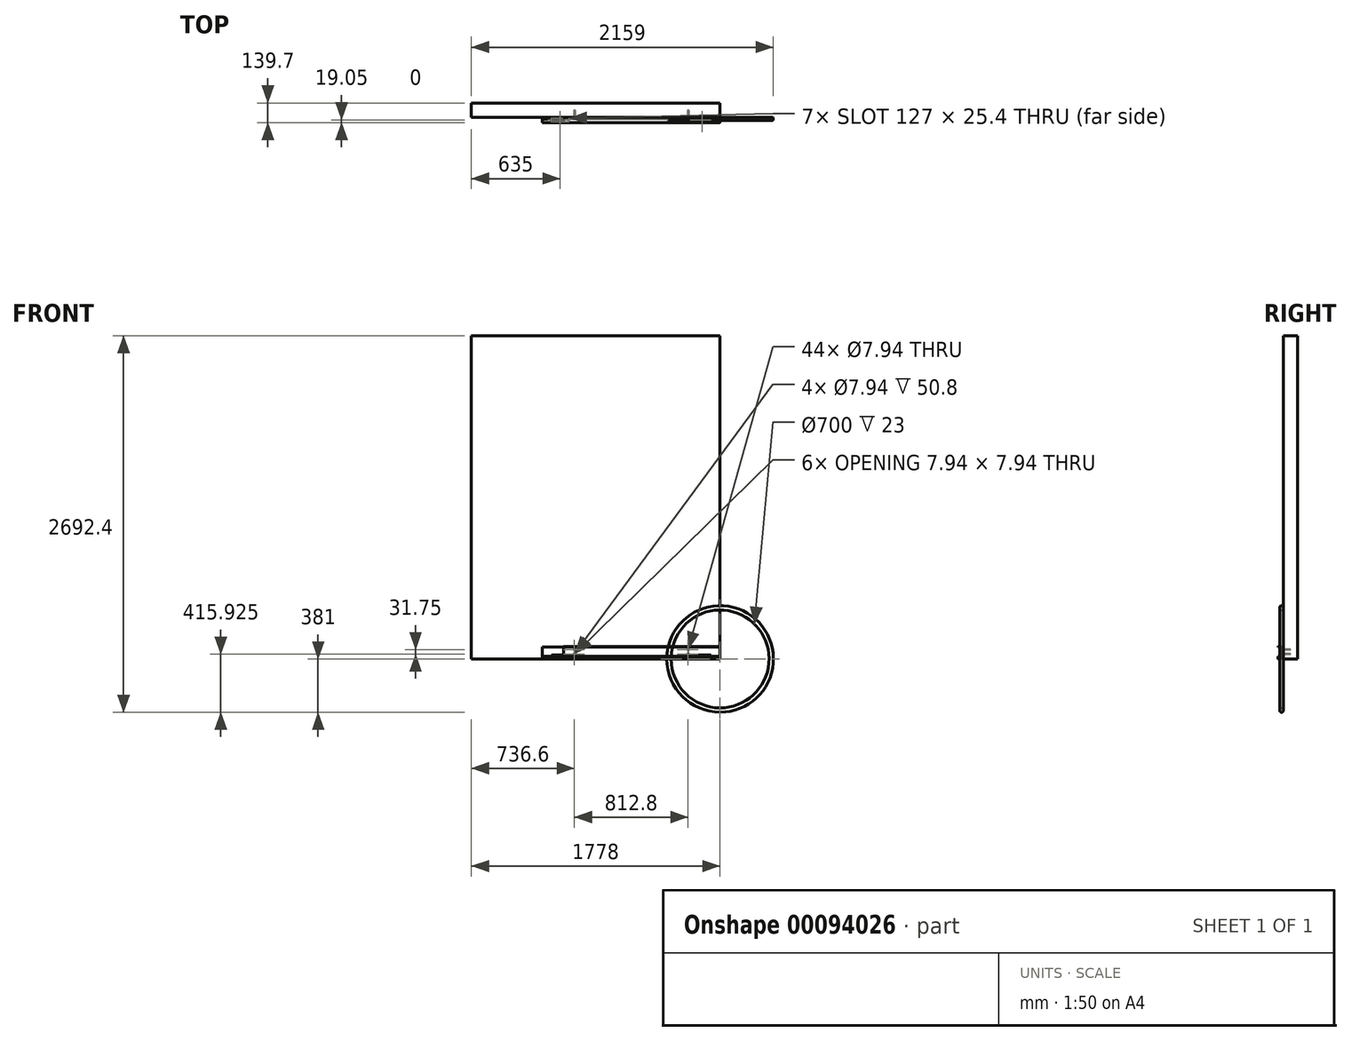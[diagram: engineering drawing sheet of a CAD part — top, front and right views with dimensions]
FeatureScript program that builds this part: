
annotation { "Feature Type Name" : "Feature", "Feature Type Description" : "" }
export const myFeature = defineFeature(function(context is Context, id is Id, definition is map)
    precondition{}
    {
        {
            var Q0;
            Q0=qCreatedBy(makeId("Right.planeOp"),FACE);
            var sketch = newSketch(context, id + "F0", { "sketchPlane" : qUnion([Q0])});
            skLineSegment(sketch, "E0", {"start": v(0, 3.17) * mm, "end": v(0, 85.73) * mm});
            skLineSegment(sketch, "E1", {"start": v(-3.18, 88.9) * mm, "end": v(-12.7, 88.9) * mm, "construction": true});
            skLineSegment(sketch, "E2", {"start": v(-12.7, 88.9) * mm, "end": v(-12.7, 85.73) * mm, "construction": true});
            skLineSegment(sketch, "E3", {"start": v(-25.4, 19.05) * mm, "end": v(-38.1, 19.05) * mm});
            skLineSegment(sketch, "E4", {"start": v(-38.1, 19.05) * mm, "end": v(-38.1, 3.18) * mm});
            skLineSegment(sketch, "E5", {"start": v(-34.92, 0) * mm, "end": v(-3.17, 0) * mm, "construction": true});
            skPoint(sketch, "E6.visualSharp", {"position": v(-12.7, 19.05) * mm});
            skArc(sketch, "E6.filletArc", {"start": v(-25.4, 19.05) * mm, "mid": v(-16.42, 22.77) * mm, "end": v(-12.7, 31.75) * mm});
            skPoint(sketch, "E7.visualSharp", {"position": v(-38.1, 0) * mm});
            skArc(sketch, "E7.filletArc", {"start": v(-38.1, 3.18) * mm, "mid": v(-37.17, 0.93) * mm, "end": v(-34.92, 0) * mm, "construction": true});
            skPoint(sketch, "E8.visualSharp", {"position": v(0, 0) * mm});
            skArc(sketch, "E8.filletArc", {"start": v(-3.18, 0) * mm, "mid": v(-0.93, 0.93) * mm, "end": v(0, 3.17) * mm, "construction": true});
            skPoint(sketch, "E9.visualSharp", {"position": v(0, 88.9) * mm});
            skArc(sketch, "E9.filletArc", {"start": v(0, 85.73) * mm, "mid": v(-0.93, 87.97) * mm, "end": v(-3.18, 88.9) * mm, "construction": true});
            skLineSegment(sketch, "E10", {"start": v(0, 85.73) * mm, "end": v(-12.7, 85.73) * mm});
            skLineSegment(sketch, "E11", {"start": v(-12.7, 85.73) * mm, "end": v(-12.7, 31.75) * mm});
            skLineSegment(sketch, "E12", {"start": v(-38.1, 3.18) * mm, "end": v(0, 3.17) * mm});
            skSolve(sketch);
        }
        {
            var Q0;
            Q0=makeQuery(id+"F0.imprint","IMPRINT",FACE,{"disambiguationData":[TD([[makeQuery(id+"F0.imprint","IMPRINT",EDGE,{"derivedFrom":sQuery(id+"F0.wireOp",EDGE,"E0")}),1.0]])]});
            extrude(context, id + "F1", {"entities" : qUnion([Q0]), "oppositeDirection" : true, "depth" : 1270 * mm});
        }
        {
            var Q0;
            Q0=qCreatedBy(makeId("Right.planeOp"),FACE);
            var sketch = newSketch(context, id + "F2", { "sketchPlane" : qUnion([Q0])});
            skLineSegment(sketch, "E13.bottom", {"start": v(-3.18, 0) * mm, "end": v(-34.93, 0) * mm});
            skLineSegment(sketch, "E13.top", {"start": v(-3.18, 88.9) * mm, "end": v(-34.93, 88.9) * mm});
            skLineSegment(sketch, "E13.left", {"start": v(0, 3.18) * mm, "end": v(0, 85.73) * mm});
            skLineSegment(sketch, "E13.right", {"start": v(-38.1, 3.18) * mm, "end": v(-38.1, 85.73) * mm});
            skPoint(sketch, "E14.visualSharp", {"position": v(-38.1, 88.9) * mm});
            skArc(sketch, "E14.filletArc", {"start": v(-34.93, 88.9) * mm, "mid": v(-37.17, 87.97) * mm, "end": v(-38.1, 85.73) * mm});
            skPoint(sketch, "E15.visualSharp", {"position": v(0, 88.9) * mm});
            skArc(sketch, "E15.filletArc", {"start": v(0, 85.73) * mm, "mid": v(-0.93, 87.97) * mm, "end": v(-3.18, 88.9) * mm});
            skPoint(sketch, "E16.visualSharp", {"position": v(0, 0) * mm});
            skArc(sketch, "E16.filletArc", {"start": v(-3.18, 0) * mm, "mid": v(-0.93, 0.93) * mm, "end": v(0, 3.18) * mm});
            skPoint(sketch, "E17.visualSharp", {"position": v(-38.1, 0) * mm});
            skArc(sketch, "E17.filletArc", {"start": v(-38.1, 3.17) * mm, "mid": v(-37.17, 0.93) * mm, "end": v(-34.93, 0) * mm});
            skSolve(sketch);
        }
        {
            var Q0;
            Q0 = qSketchRegion(id + "F2", true);
            extrude(context, id + "F3", {"entities" : qUnion([Q0]), "oppositeDirection" : true, "depth" : 1117.6 * mm});
        }
        {
            var Q0;
            Q0=qCreatedBy(makeId("Right.planeOp"),FACE);
            var sketch = newSketch(context, id + "F4", { "sketchPlane" : qUnion([Q0])});
            skLineSegment(sketch, "E18.bottom", {"start": v(-3.18, 0) * mm, "end": v(-34.93, 0) * mm, "construction": true});
            skLineSegment(sketch, "E18.top", {"start": v(-3.18, 88.9) * mm, "end": v(-34.93, 88.9) * mm, "construction": true});
            skLineSegment(sketch, "E18.left", {"start": v(0, 3.17) * mm, "end": v(0, 85.73) * mm});
            skLineSegment(sketch, "E18.right", {"start": v(-38.1, 3.17) * mm, "end": v(-38.1, 85.73) * mm});
            skPoint(sketch, "E19.visualSharp", {"position": v(-38.1, 88.9) * mm});
            skArc(sketch, "E19.filletArc", {"start": v(-34.93, 88.9) * mm, "mid": v(-37.17, 87.97) * mm, "end": v(-38.1, 85.73) * mm, "construction": true});
            skPoint(sketch, "E20.visualSharp", {"position": v(0, 88.9) * mm});
            skArc(sketch, "E20.filletArc", {"start": v(0, 85.73) * mm, "mid": v(-0.93, 87.97) * mm, "end": v(-3.18, 88.9) * mm, "construction": true});
            skPoint(sketch, "E21.visualSharp", {"position": v(0, 0) * mm});
            skArc(sketch, "E21.filletArc", {"start": v(-3.18, 0) * mm, "mid": v(-0.93, 0.93) * mm, "end": v(0, 3.17) * mm, "construction": true});
            skPoint(sketch, "E22.visualSharp", {"position": v(-38.1, 0) * mm});
            skArc(sketch, "E22.filletArc", {"start": v(-38.1, 3.17) * mm, "mid": v(-37.17, 0.93) * mm, "end": v(-34.93, 0) * mm, "construction": true});
            skLineSegment(sketch, "E23", {"start": v(-38.1, 85.73) * mm, "end": v(0, 85.73) * mm});
            skLineSegment(sketch, "E24", {"start": v(-38.1, 3.17) * mm, "end": v(0, 3.17) * mm});
            skSolve(sketch);
        }
        {
            var Q0;
            Q0 = qSketchRegion(id + "F4", true);
            extrude(context, id + "F5", {"entities" : qUnion([Q0]), "oppositeDirection" : true, "depth" : 1117.6 * mm});
        }
        {
            var Q0;
            Q0=makeQuery(id+"F5.opExtrude","SWEPT_BODY",BODY,{"disambiguationData":[OSD([sQuery(id+"F4.wireOp",EDGE,"E18.left"),sQuery(id+"F4.wireOp",EDGE,"E18.right"),sQuery(id+"F4.wireOp",EDGE,"E23"),sQuery(id+"F4.wireOp",EDGE,"E24")])]});
            transform(context, id + "F6", {"entities" : qUnion([Q0]), "transformType" : TransformType.TRANSLATION_3D, "dx" : 0 * mm, "dy" : 0 * mm, "dz" : 0 * mm, "makeCopy" : true});
        }
        {
            var Q0;
            Q0=makeQuery(id+"F6.opPattern","COPY",FACE,{"derivedFrom":makeQuery(id+"F5.opExtrude","CAP_FACE",FACE,{"disambiguationData":[OSD([sQuery(id+"F4.wireOp",EDGE,"E18.left"),sQuery(id+"F4.wireOp",EDGE,"E18.right"),sQuery(id+"F4.wireOp",EDGE,"E23"),sQuery(id+"F4.wireOp",EDGE,"E24")])],"isStart":true}),"instanceName":"1"});
            var sketch = newSketch(context, id + "F7", { "sketchPlane" : qUnion([Q0])});
            skLineSegment(sketch, "E25", {"start": v(-38.1, 3.17) * mm, "end": v(-38.1, 31.75) * mm, "construction": true});
            skLineSegment(sketch, "E26", {"start": v(-38.1, 31.75) * mm, "end": v(-14.29, 31.75) * mm});
            skLineSegment(sketch, "E27", {"start": v(-14.29, 31.75) * mm, "end": v(-14.29, 85.73) * mm});
            skLineSegment(sketch, "E28", {"start": v(-14.29, 85.73) * mm, "end": v(-38.1, 85.73) * mm});
            skLineSegment(sketch, "E29", {"start": v(-38.1, 85.73) * mm, "end": v(-38.1, 31.75) * mm});
            skSolve(sketch);
        }
        {
            var Q0;
            Q0 = qSketchRegion(id + "F7", true);
            extrude(context, id + "F8", {"entities" : qUnion([Q0]), "operationType" : NewBodyOperationType.REMOVE, "endBound" : BoundingType.THROUGH_ALL, "oppositeDirection" : true, "depth" : 25.4 * mm});
        }
        {
            var Q0;
            Q0=makeQuery(id+"F1.opExtrude","SWEPT_BODY",BODY,{"disambiguationData":[OSD([sQuery(id+"F0.wireOp",EDGE,"E0"),sQuery(id+"F0.wireOp",EDGE,"E3"),sQuery(id+"F0.wireOp",EDGE,"E4"),sQuery(id+"F0.wireOp",EDGE,"E6.filletArc"),sQuery(id+"F0.wireOp",EDGE,"E10"),sQuery(id+"F0.wireOp",EDGE,"E11"),sQuery(id+"F0.wireOp",EDGE,"E12")])]});
            transform(context, id + "F9", {"entities" : qUnion([Q0]), "transformType" : TransformType.TRANSLATION_3D, "dx" : 0 * mm, "dy" : 0 * mm, "dz" : 0 * mm, "makeCopy" : true});
        }
        {
            var Q0;
            Q0=makeQuery(id+"F9.opPattern","COPY",FACE,{"derivedFrom":makeQuery(id+"F1.opExtrude","CAP_FACE",FACE,{"disambiguationData":[OSD([sQuery(id+"F0.wireOp",EDGE,"E0"),sQuery(id+"F0.wireOp",EDGE,"E3"),sQuery(id+"F0.wireOp",EDGE,"E4"),sQuery(id+"F0.wireOp",EDGE,"E6.filletArc"),sQuery(id+"F0.wireOp",EDGE,"E10"),sQuery(id+"F0.wireOp",EDGE,"E11"),sQuery(id+"F0.wireOp",EDGE,"E12")])],"isStart":true}),"instanceName":"1"});
            var sketch = newSketch(context, id + "F10", { "sketchPlane" : qUnion([Q0])});
            skLineSegment(sketch, "E30", {"start": v(-25.4, 19.05) * mm, "end": v(-12.7, 19.05) * mm});
            skLineSegment(sketch, "E31", {"start": v(-12.7, 19.05) * mm, "end": v(-12.7, 31.75) * mm});
            skLineSegment(sketch, "E32", {"start": v(-12.7, 31.75) * mm, "end": v(-25.4, 31.75) * mm});
            skLineSegment(sketch, "E33", {"start": v(-25.4, 31.75) * mm, "end": v(-25.4, 19.05) * mm});
            skSolve(sketch);
        }
        {
            var Q0;
            Q0 = qSketchRegion(id + "F10", true);
            extrude(context, id + "F11", {"entities" : qUnion([Q0]), "operationType" : NewBodyOperationType.REMOVE, "endBound" : BoundingType.THROUGH_ALL, "oppositeDirection" : true, "depth" : 25.4 * mm});
        }
        {
            var Q0;
            Q0=makeQuery(id+"F1.opExtrude","SWEPT_BODY",BODY,{"disambiguationData":[OSD([sQuery(id+"F0.wireOp",EDGE,"E0"),sQuery(id+"F0.wireOp",EDGE,"E3"),sQuery(id+"F0.wireOp",EDGE,"E4"),sQuery(id+"F0.wireOp",EDGE,"E6.filletArc"),sQuery(id+"F0.wireOp",EDGE,"E10"),sQuery(id+"F0.wireOp",EDGE,"E11"),sQuery(id+"F0.wireOp",EDGE,"E12")])]});
            transform(context, id + "F12", {"entities" : qUnion([Q0]), "transformType" : TransformType.TRANSLATION_3D, "dx" : 0 * mm, "dy" : 0 * mm, "dz" : 0 * mm, "makeCopy" : true});
        }
        {
            var Q0;
            Q0=makeQuery(id+"F12.opPattern","COPY",FACE,{"derivedFrom":makeQuery(id+"F1.opExtrude","CAP_FACE",FACE,{"disambiguationData":[OSD([sQuery(id+"F0.wireOp",EDGE,"E0"),sQuery(id+"F0.wireOp",EDGE,"E3"),sQuery(id+"F0.wireOp",EDGE,"E4"),sQuery(id+"F0.wireOp",EDGE,"E6.filletArc"),sQuery(id+"F0.wireOp",EDGE,"E10"),sQuery(id+"F0.wireOp",EDGE,"E11"),sQuery(id+"F0.wireOp",EDGE,"E12")])],"isStart":true}),"instanceName":"1"});
            var sketch = newSketch(context, id + "F13", { "sketchPlane" : qUnion([Q0])});
            skLineSegment(sketch, "E34", {"start": v(-25.4, 19.05) * mm, "end": v(-19.05, 19.05) * mm});
            skLineSegment(sketch, "E35", {"start": v(-12.7, 25.4) * mm, "end": v(-12.7, 31.75) * mm});
            skLineSegment(sketch, "E36", {"start": v(-12.7, 31.75) * mm, "end": v(-25.4, 31.75) * mm});
            skLineSegment(sketch, "E37", {"start": v(-25.4, 31.75) * mm, "end": v(-25.4, 19.05) * mm});
            skPoint(sketch, "E38.visualSharp", {"position": v(-12.7, 19.05) * mm});
            skArc(sketch, "E38.filletArc", {"start": v(-19.05, 19.05) * mm, "mid": v(-14.56, 20.9) * mm, "end": v(-12.7, 25.4) * mm});
            skSolve(sketch);
        }
        {
            var Q0;
            Q0 = qSketchRegion(id + "F13", true);
            extrude(context, id + "F14", {"entities" : qUnion([Q0]), "operationType" : NewBodyOperationType.REMOVE, "endBound" : BoundingType.THROUGH_ALL, "oppositeDirection" : true, "depth" : 25.4 * mm});
        }
        {
            var Q0;
            Q0=makeQuery(id+"F6.opPattern","COPY",BODY,{"derivedFrom":makeQuery(id+"F5.opExtrude","SWEPT_BODY",BODY,{"disambiguationData":[OSD([sQuery(id+"F4.wireOp",EDGE,"E18.left"),sQuery(id+"F4.wireOp",EDGE,"E18.right"),sQuery(id+"F4.wireOp",EDGE,"E23"),sQuery(id+"F4.wireOp",EDGE,"E24")])]}),"instanceName":"1"});
            transform(context, id + "F15", {"entities" : qUnion([Q0]), "transformType" : TransformType.TRANSLATION_3D, "dx" : 0 * mm, "dy" : 0 * mm, "dz" : 0 * mm, "makeCopy" : true});
        }
        {
            var Q0;
            Q0=makeQuery(id+"F15.opPattern","COPY",FACE,{"derivedFrom":makeQuery(id+"F6.opPattern","COPY",FACE,{"derivedFrom":makeQuery(id+"F5.opExtrude","CAP_FACE",FACE,{"disambiguationData":[OSD([sQuery(id+"F4.wireOp",EDGE,"E18.left"),sQuery(id+"F4.wireOp",EDGE,"E18.right"),sQuery(id+"F4.wireOp",EDGE,"E23"),sQuery(id+"F4.wireOp",EDGE,"E24")])],"isStart":true}),"instanceName":"1"}),"instanceName":"1"});
            var sketch = newSketch(context, id + "F16", { "sketchPlane" : qUnion([Q0])});
            skCircle(sketch, "E39", {"center": v(-38.1, 31.75) * mm, "radius": 12.7 * mm});
            skSolve(sketch);
        }
        {
            var Q0;
            Q0 = qSketchRegion(id + "F16", true);
            extrude(context, id + "F17", {"entities" : qUnion([Q0]), "operationType" : NewBodyOperationType.REMOVE, "endBound" : BoundingType.THROUGH_ALL, "oppositeDirection" : true, "depth" : 25.4 * mm});
        }
        {
            var Q0;
            Q0=makeQuery(id+"F15.opPattern","COPY",BODY,{"derivedFrom":makeQuery(id+"F6.opPattern","COPY",BODY,{"derivedFrom":makeQuery(id+"F5.opExtrude","SWEPT_BODY",BODY,{"disambiguationData":[OSD([sQuery(id+"F4.wireOp",EDGE,"E18.left"),sQuery(id+"F4.wireOp",EDGE,"E18.right"),sQuery(id+"F4.wireOp",EDGE,"E23"),sQuery(id+"F4.wireOp",EDGE,"E24")])]}),"instanceName":"1"}),"instanceName":"1"});
            transform(context, id + "F18", {"entities" : qUnion([Q0]), "transformType" : TransformType.TRANSLATION_3D, "dx" : 0 * mm, "dy" : 0 * mm, "dz" : 0 * mm, "makeCopy" : true});
        }
        {
            var Q0;
            Q0=makeQuery(id+"F18.opPattern","COPY",FACE,{"derivedFrom":makeQuery(id+"F15.opPattern","COPY",FACE,{"derivedFrom":makeQuery(id+"F6.opPattern","COPY",FACE,{"derivedFrom":makeQuery(id+"F5.opExtrude","CAP_FACE",FACE,{"disambiguationData":[OSD([sQuery(id+"F4.wireOp",EDGE,"E18.left"),sQuery(id+"F4.wireOp",EDGE,"E18.right"),sQuery(id+"F4.wireOp",EDGE,"E23"),sQuery(id+"F4.wireOp",EDGE,"E24")])],"isStart":true}),"instanceName":"1"}),"instanceName":"1"}),"instanceName":"1"});
            var sketch = newSketch(context, id + "F19", { "sketchPlane" : qUnion([Q0])});
            skCircle(sketch, "E40", {"center": v(-25.4, 31.75) * mm, "radius": 12.7 * mm});
            skSolve(sketch);
        }
        {
            var Q0;
            Q0 = qSketchRegion(id + "F19", true);
            extrude(context, id + "F20", {"entities" : qUnion([Q0]), "operationType" : NewBodyOperationType.REMOVE, "endBound" : BoundingType.THROUGH_ALL, "oppositeDirection" : true, "depth" : 25.4 * mm});
        }
        {
            var Q0;
            Q0=makeQuery(id+"F18.opPattern","COPY",BODY,{"derivedFrom":makeQuery(id+"F15.opPattern","COPY",BODY,{"derivedFrom":makeQuery(id+"F6.opPattern","COPY",BODY,{"derivedFrom":makeQuery(id+"F5.opExtrude","SWEPT_BODY",BODY,{"disambiguationData":[OSD([sQuery(id+"F4.wireOp",EDGE,"E18.left"),sQuery(id+"F4.wireOp",EDGE,"E18.right"),sQuery(id+"F4.wireOp",EDGE,"E23"),sQuery(id+"F4.wireOp",EDGE,"E24")])]}),"instanceName":"1"}),"instanceName":"1"}),"instanceName":"1"});
            transform(context, id + "F21", {"entities" : qUnion([Q0]), "transformType" : TransformType.TRANSLATION_3D, "dx" : 0 * mm, "dy" : 0 * mm, "dz" : 0 * mm, "makeCopy" : true});
        }
        {
            var Q0;
            Q0=makeQuery(id+"F21.opPattern","COPY",FACE,{"derivedFrom":makeQuery(id+"F18.opPattern","COPY",FACE,{"derivedFrom":makeQuery(id+"F15.opPattern","COPY",FACE,{"derivedFrom":makeQuery(id+"F6.opPattern","COPY",FACE,{"derivedFrom":makeQuery(id+"F5.opExtrude","CAP_FACE",FACE,{"disambiguationData":[OSD([sQuery(id+"F4.wireOp",EDGE,"E18.left"),sQuery(id+"F4.wireOp",EDGE,"E18.right"),sQuery(id+"F4.wireOp",EDGE,"E23"),sQuery(id+"F4.wireOp",EDGE,"E24")])],"isStart":true}),"instanceName":"1"}),"instanceName":"1"}),"instanceName":"1"}),"instanceName":"1"});
            var sketch = newSketch(context, id + "F22", { "sketchPlane" : qUnion([Q0])});
            skLineSegment(sketch, "E41", {"start": v(-38.1, 19.05) * mm, "end": v(-25.4, 19.05) * mm});
            skLineSegment(sketch, "E42", {"start": v(-25.4, 19.05) * mm, "end": v(-25.4, 31.75) * mm});
            skLineSegment(sketch, "E43", {"start": v(-38.1, 19.05) * mm, "end": v(-38.1, 31.75) * mm});
            skLineSegment(sketch, "E44", {"start": v(-38.1, 31.75) * mm, "end": v(-25.4, 31.75) * mm});
            skSolve(sketch);
        }
        {
            var Q0;
            Q0 = qSketchRegion(id + "F22", true);
            extrude(context, id + "F23", {"entities" : qUnion([Q0]), "operationType" : NewBodyOperationType.REMOVE, "endBound" : BoundingType.THROUGH_ALL, "oppositeDirection" : true, "depth" : 25.4 * mm});
        }
        {
            var Q0;
            Q0=makeQuery(id+"F21.opPattern","COPY",BODY,{"derivedFrom":makeQuery(id+"F18.opPattern","COPY",BODY,{"derivedFrom":makeQuery(id+"F15.opPattern","COPY",BODY,{"derivedFrom":makeQuery(id+"F6.opPattern","COPY",BODY,{"derivedFrom":makeQuery(id+"F5.opExtrude","SWEPT_BODY",BODY,{"disambiguationData":[OSD([sQuery(id+"F4.wireOp",EDGE,"E18.left"),sQuery(id+"F4.wireOp",EDGE,"E18.right"),sQuery(id+"F4.wireOp",EDGE,"E23"),sQuery(id+"F4.wireOp",EDGE,"E24")])]}),"instanceName":"1"}),"instanceName":"1"}),"instanceName":"1"}),"instanceName":"1"});
            transform(context, id + "F24", {"entities" : qUnion([Q0]), "transformType" : TransformType.TRANSLATION_3D, "dx" : 0 * mm, "dy" : 0 * mm, "dz" : 0 * mm, "makeCopy" : true});
        }
        {
            var Q0;
            Q0=makeQuery(id+"F24.opPattern","COPY",FACE,{"derivedFrom":makeQuery(id+"F21.opPattern","COPY",FACE,{"derivedFrom":makeQuery(id+"F18.opPattern","COPY",FACE,{"derivedFrom":makeQuery(id+"F15.opPattern","COPY",FACE,{"derivedFrom":makeQuery(id+"F6.opPattern","COPY",FACE,{"derivedFrom":makeQuery(id+"F5.opExtrude","CAP_FACE",FACE,{"disambiguationData":[OSD([sQuery(id+"F4.wireOp",EDGE,"E18.left"),sQuery(id+"F4.wireOp",EDGE,"E18.right"),sQuery(id+"F4.wireOp",EDGE,"E23"),sQuery(id+"F4.wireOp",EDGE,"E24")])],"isStart":true}),"instanceName":"1"}),"instanceName":"1"}),"instanceName":"1"}),"instanceName":"1"}),"instanceName":"1"});
            var sketch = newSketch(context, id + "F25", { "sketchPlane" : qUnion([Q0])});
            skLineSegment(sketch, "E45.bottom", {"start": v(-14.29, 85.73) * mm, "end": v(-12.7, 85.73) * mm});
            skLineSegment(sketch, "E45.top", {"start": v(-14.29, 31.75) * mm, "end": v(-12.7, 31.75) * mm});
            skLineSegment(sketch, "E45.left", {"start": v(-14.29, 85.73) * mm, "end": v(-14.29, 31.75) * mm});
            skLineSegment(sketch, "E45.right", {"start": v(-12.7, 85.73) * mm, "end": v(-12.7, 31.75) * mm});
            skSolve(sketch);
        }
        {
            var Q0;
            Q0 = qSketchRegion(id + "F25", true);
            extrude(context, id + "F26", {"entities" : qUnion([Q0]), "operationType" : NewBodyOperationType.REMOVE, "endBound" : BoundingType.THROUGH_ALL, "oppositeDirection" : true, "depth" : 25.4 * mm});
        }
        {
            var Q0;
            Q0=qCreatedBy(makeId("Front.planeOp"),FACE);
            var sketch = newSketch(context, id + "F27", { "sketchPlane" : qUnion([Q0])});
            skLineSegment(sketch, "E46.bottom", {"start": v(0, 0) * mm, "end": v(-1778, 0) * mm});
            skLineSegment(sketch, "E46.top", {"start": v(0, 2311.4) * mm, "end": v(-1778, 2311.4) * mm});
            skLineSegment(sketch, "E46.left", {"start": v(0, 0) * mm, "end": v(0, 2311.4) * mm});
            skLineSegment(sketch, "E46.right", {"start": v(-1778, 0) * mm, "end": v(-1778, 2311.4) * mm});
            skSolve(sketch);
        }
        {
            var Q0;
            Q0 = qSketchRegion(id + "F27", true);
            extrude(context, id + "F28", {"entities" : qUnion([Q0]), "oppositeDirection" : true, "depth" : 101.6 * mm});
        }
        {
            var Q0;
            Q0=qCreatedBy(makeId("Front.planeOp"),FACE);
            var sketch = newSketch(context, id + "F29", { "sketchPlane" : qUnion([Q0])});
            skCircle(sketch, "E47", {"center": v(0, 0) * mm, "radius": 350 * mm});
            skCircle(sketch, "E48", {"center": v(0, 0) * mm, "radius": 381 * mm});
            skSolve(sketch);
        }
        {
            var Q0;
            Q0 = qSketchRegion(id + "F29", true);
            extrude(context, id + "F30", {"entities" : qUnion([Q0]), "depth" : 23 * mm});
        }
        {
            var Q0;
            Q0=makeQuery(id+"F30.opExtrude","CAP_EDGE",EDGE,{"disambiguationData":[OSD([sQuery(id+"F29.wireOp",EDGE,"E48")])],"isStart":false});
            var Q1;
            Q1=makeQuery(id+"F30.opExtrude","CAP_EDGE",EDGE,{"disambiguationData":[OSD([sQuery(id+"F29.wireOp",EDGE,"E48")])],"isStart":true});
            fillet(context, id + "F31", {"entities" : qUnion([Q0, Q1]), "radius" : 10.16 * mm, "tangentPropagation" : true, "allowEdgeOverflow" : false});
        }
        {
            var Q0;
            Q0=qCreatedBy(makeId("Right.planeOp"),FACE);
            var sketch = newSketch(context, id + "F32", { "sketchPlane" : qUnion([Q0])});
            skLineSegment(sketch, "E49.bottom", {"start": v(0, 0) * mm, "end": v(-38.1, 0) * mm, "construction": true});
            skLineSegment(sketch, "E49.top", {"start": v(0, 88.9) * mm, "end": v(-38.1, 88.9) * mm, "construction": true});
            skLineSegment(sketch, "E49.left", {"start": v(0, 0) * mm, "end": v(0, 3.18) * mm, "construction": true});
            skLineSegment(sketch, "E49.right", {"start": v(-38.1, 0) * mm, "end": v(-38.1, 3.17) * mm, "construction": true});
            skLineSegment(sketch, "E50.0", {"start": v(0, 85.73) * mm, "end": v(-12.7, 85.73) * mm});
            skLineSegment(sketch, "E51", {"start": v(-38.1, 85.73) * mm, "end": v(-38.1, 88.9) * mm, "construction": true});
            skLineSegment(sketch, "E52", {"start": v(0, 85.73) * mm, "end": v(0, 88.9) * mm});
            skLineSegment(sketch, "E53.0", {"start": v(0, 3.18) * mm, "end": v(-38.1, 3.17) * mm});
            skLineSegment(sketch, "E54", {"start": v(-38.1, 3.17) * mm, "end": v(-38.1, 19.05) * mm});
            skLineSegment(sketch, "E55", {"start": v(0, 3.18) * mm, "end": v(0, 85.73) * mm});
            skLineSegment(sketch, "E56", {"start": v(-12.7, 85.73) * mm, "end": v(-12.7, 31.75) * mm});
            skLineSegment(sketch, "E57", {"start": v(-25.4, 19.05) * mm, "end": v(-38.1, 19.05) * mm});
            skPoint(sketch, "E58.visualSharp", {"position": v(-12.7, 19.05) * mm});
            skArc(sketch, "E58.filletArc", {"start": v(-25.4, 19.05) * mm, "mid": v(-16.42, 22.77) * mm, "end": v(-12.7, 31.75) * mm});
            skLineSegment(sketch, "E59", {"start": v(-38.1, 19.05) * mm, "end": v(-38.1, 85.73) * mm, "construction": true});
            skLineSegment(sketch, "E60", {"start": v(-12.7, 85.73) * mm, "end": v(-38.1, 85.73) * mm, "construction": true});
            skSolve(sketch);
        }
        {
            var Q0;
            Q0 = qSketchRegion(id + "F32", true);
            extrude(context, id + "F33", {"entities" : qUnion([Q0]), "oppositeDirection" : true, "depth" : 1270 * mm});
        }
        {
            var Q0;
            Q0=qCreatedBy(makeId("Front.planeOp"),FACE);
            var sketch = newSketch(context, id + "F34", { "sketchPlane" : qUnion([Q0])});
            skCircle(sketch, "E61", {"center": v(-228.6, 66.68) * mm, "radius": 3.97 * mm});
            skCircle(sketch, "E62.0.1.0", {"center": v(-228.6, 34.93) * mm, "radius": 3.97 * mm});
            skCircle(sketch, "E62.1.0.0", {"center": v(-1041.4, 66.68) * mm, "radius": 3.97 * mm});
            skCircle(sketch, "E62.1.1.0", {"center": v(-1041.4, 34.93) * mm, "radius": 3.97 * mm});
            skLineSegment(sketch, "E62.direction1", {"start": v(-228.6, 66.67) * mm, "end": v(-1041.4, 66.67) * mm, "construction": true});
            skLineSegment(sketch, "E62.direction2", {"start": v(-228.6, 66.68) * mm, "end": v(-228.6, 34.93) * mm, "construction": true});
            skSolve(sketch);
        }
        {
            var Q0;
            Q0 = qSketchRegion(id + "F34", true);
            extrude(context, id + "F35", {"entities" : qUnion([Q0]), "operationType" : NewBodyOperationType.REMOVE, "endBound" : BoundingType.SYMMETRIC, "oppositeDirection" : true, "depth" : 101.6 * mm});
        }
        {
            var Q0;
            Q0=makeQuery(id+"F33.opExtrude","SWEPT_FACE",FACE,{"disambiguationData":[OSD([sQuery(id+"F32.wireOp",EDGE,"E53.0")])]});
            var sketch = newSketch(context, id + "F36", { "sketchPlane" : qUnion([Q0])});
            skLineSegment(sketch, "E63.bottom", {"start": v(-1193.8, 31.75) * mm, "end": v(-1092.2, 31.75) * mm});
            skLineSegment(sketch, "E63.top", {"start": v(-1193.8, 6.35) * mm, "end": v(-1092.2, 6.35) * mm});
            skLineSegment(sketch, "E63.left", {"start": v(-1206.5, 19.05) * mm, "end": v(-1206.5, 19.05) * mm});
            skLineSegment(sketch, "E63.right", {"start": v(-1079.5, 19.05) * mm, "end": v(-1079.5, 19.05) * mm});
            skPoint(sketch, "E64.visualSharp", {"position": v(-1206.5, 31.75) * mm});
            skArc(sketch, "E64.filletArc", {"start": v(-1193.8, 31.75) * mm, "mid": v(-1202.78, 28.03) * mm, "end": v(-1206.5, 19.05) * mm});
            skPoint(sketch, "E65.visualSharp", {"position": v(-1206.5, 6.35) * mm});
            skArc(sketch, "E65.filletArc", {"start": v(-1206.5, 19.05) * mm, "mid": v(-1202.78, 10.07) * mm, "end": v(-1193.8, 6.35) * mm});
            skPoint(sketch, "E66.visualSharp", {"position": v(-1079.5, 31.75) * mm});
            skArc(sketch, "E66.filletArc", {"start": v(-1079.5, 19.05) * mm, "mid": v(-1083.22, 28.03) * mm, "end": v(-1092.2, 31.75) * mm});
            skPoint(sketch, "E67.visualSharp", {"position": v(-1079.5, 6.35) * mm});
            skArc(sketch, "E67.filletArc", {"start": v(-1092.2, 6.35) * mm, "mid": v(-1083.22, 10.07) * mm, "end": v(-1079.5, 19.05) * mm});
            skLineSegment(sketch, "E68", {"start": v(-635, 38.1) * mm, "end": v(-635, 0) * mm, "construction": true});
            skArc(sketch, "E69.MirrorCS", {"start": v(-76.2, 31.75) * mm, "mid": v(-67.22, 28.03) * mm, "end": v(-63.5, 19.05) * mm});
            skArc(sketch, "E70.MirrorCS", {"start": v(-63.5, 19.05) * mm, "mid": v(-67.22, 10.07) * mm, "end": v(-76.2, 6.35) * mm});
            skArc(sketch, "E71.MirrorCS", {"start": v(-190.5, 19.05) * mm, "mid": v(-186.78, 28.03) * mm, "end": v(-177.8, 31.75) * mm});
            skArc(sketch, "E72.MirrorCS", {"start": v(-177.8, 6.35) * mm, "mid": v(-186.78, 10.07) * mm, "end": v(-190.5, 19.05) * mm});
            skLineSegment(sketch, "E73.MirrorCS", {"start": v(-76.2, 6.35) * mm, "end": v(-177.8, 6.35) * mm});
            skLineSegment(sketch, "E74.MirrorCS", {"start": v(-76.2, 31.75) * mm, "end": v(-177.8, 31.75) * mm});
            skPoint(sketch, "E75.MirrorP", {"position": v(-63.5, 31.75) * mm});
            skLineSegment(sketch, "E76.MirrorCS", {"start": v(-190.5, 19.05) * mm, "end": v(-190.5, 19.05) * mm});
            skPoint(sketch, "E77.MirrorP", {"position": v(-190.5, 31.75) * mm});
            skPoint(sketch, "E78.MirrorP", {"position": v(-190.5, 6.35) * mm});
            skLineSegment(sketch, "E79.MirrorCS", {"start": v(-63.5, 19.05) * mm, "end": v(-63.5, 19.05) * mm});
            skPoint(sketch, "E80.MirrorP", {"position": v(-63.5, 6.35) * mm});
            skSolve(sketch);
        }
        {
            var Q0;
            Q0 = qSketchRegion(id + "F36", true);
            extrude(context, id + "F37", {"entities" : qUnion([Q0]), "operationType" : NewBodyOperationType.REMOVE, "oppositeDirection" : true, "depth" : 25.4 * mm});
        }
    });
